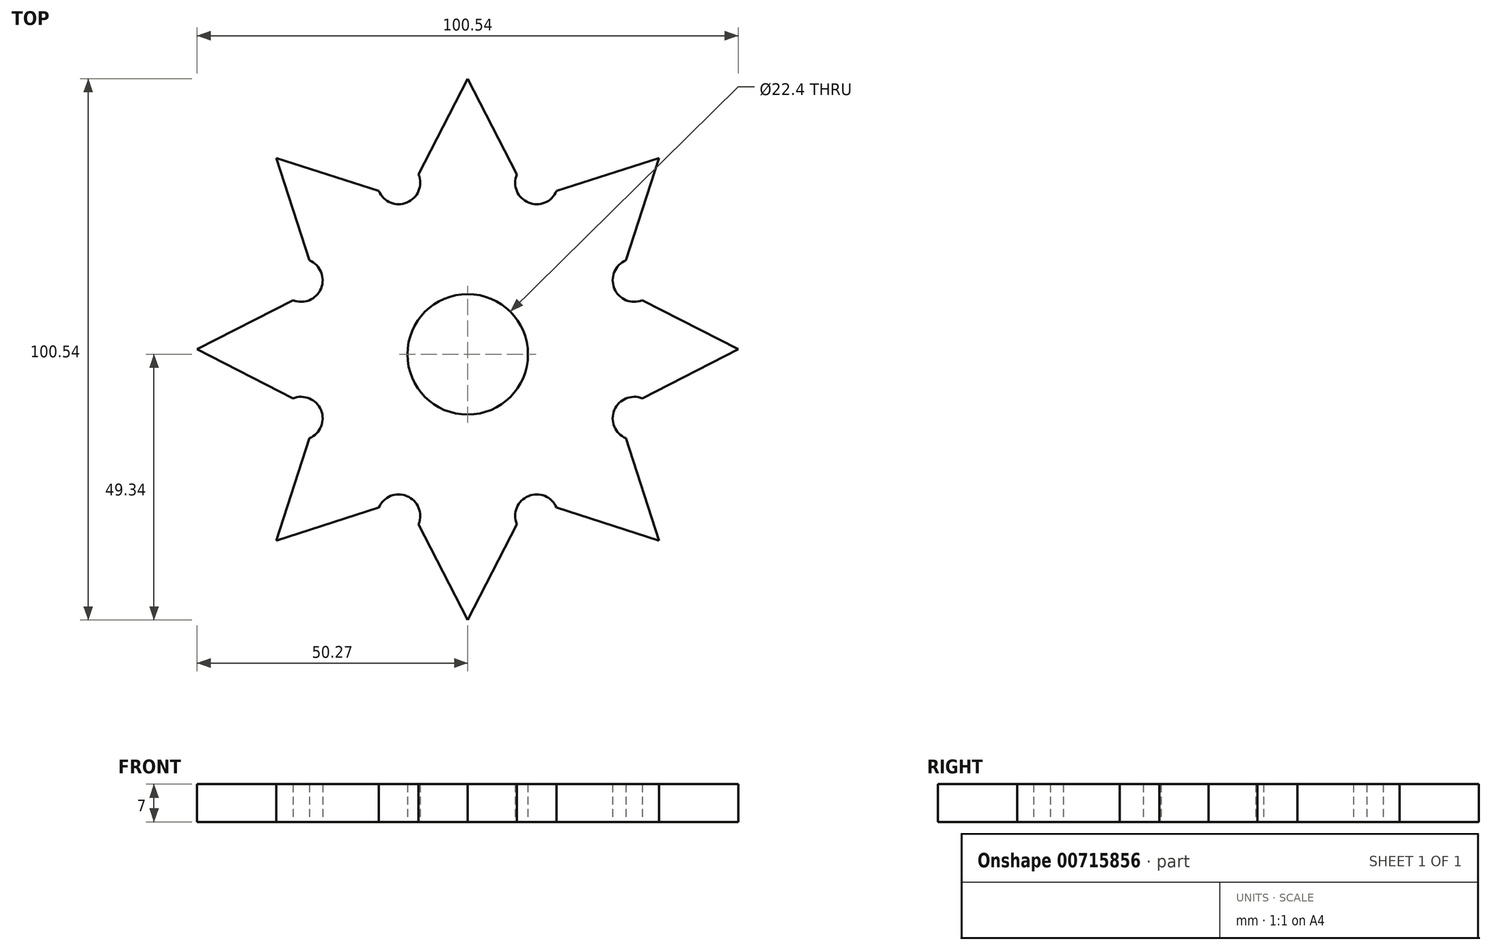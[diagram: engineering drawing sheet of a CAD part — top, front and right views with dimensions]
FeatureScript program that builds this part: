
annotation { "Feature Type Name" : "Feature", "Feature Type Description" : "" }
export const myFeature = defineFeature(function(context is Context, id is Id, definition is map)
    precondition{}
    {
        {
            var Q0;
            Q0=qCreatedBy(makeId("Top.planeOp"),FACE);
            var sketch = newSketch(context, id + "F0", { "sketchPlane" : qUnion([Q0])});
            skCircle(sketch, "E0", {"center": v(0, 0) * mm, "radius": 11.2 * mm});
            skLineSegment(sketch, "E1", {"start": v(0, 11.2) * mm, "end": v(0, 51.2) * mm});
            skLineSegment(sketch, "E2", {"start": v(0, 51.2) * mm, "end": v(9.12, 33.4) * mm});
            skLineSegment(sketch, "E3", {"start": v(0, 51.2) * mm, "end": v(-9.12, 33.4) * mm});
            skLineSegment(sketch, "E4", {"start": v(-9.12, 33.4) * mm, "end": v(0, 11.2) * mm});
            skLineSegment(sketch, "E5", {"start": v(9.12, 33.4) * mm, "end": v(0, 11.2) * mm});
            skLineSegment(sketch, "E6.1.0", {"start": v(-29.4, 17.44) * mm, "end": v(-7.26, 8.2) * mm});
            skLineSegment(sketch, "E6.1.1", {"start": v(-16.51, 30.34) * mm, "end": v(-7.26, 8.2) * mm});
            skLineSegment(sketch, "E6.1.2", {"start": v(-35.54, 36.48) * mm, "end": v(-16.51, 30.34) * mm});
            skLineSegment(sketch, "E6.1.3", {"start": v(-35.54, 36.48) * mm, "end": v(-29.4, 17.44) * mm});
            skLineSegment(sketch, "E6.2.0", {"start": v(-32.47, -8.19) * mm, "end": v(-10.27, 0.93) * mm});
            skLineSegment(sketch, "E6.2.1", {"start": v(-32.47, 10.05) * mm, "end": v(-10.27, 0.93) * mm});
            skLineSegment(sketch, "E6.2.2", {"start": v(-50.27, 0.93) * mm, "end": v(-32.47, 10.05) * mm});
            skLineSegment(sketch, "E6.2.3", {"start": v(-50.27, 0.93) * mm, "end": v(-32.47, -8.19) * mm});
            skLineSegment(sketch, "E6.3.0", {"start": v(-16.51, -28.47) * mm, "end": v(-7.26, -6.33) * mm});
            skLineSegment(sketch, "E6.3.1", {"start": v(-29.4, -15.58) * mm, "end": v(-7.26, -6.33) * mm});
            skLineSegment(sketch, "E6.3.2", {"start": v(-35.54, -34.61) * mm, "end": v(-29.4, -15.58) * mm});
            skLineSegment(sketch, "E6.3.3", {"start": v(-35.54, -34.61) * mm, "end": v(-16.51, -28.47) * mm});
            skLineSegment(sketch, "E6.4.0", {"start": v(9.12, -31.54) * mm, "end": v(0, -9.34) * mm});
            skLineSegment(sketch, "E6.4.1", {"start": v(-9.12, -31.54) * mm, "end": v(0, -9.34) * mm});
            skLineSegment(sketch, "E6.4.2", {"start": v(0, -49.34) * mm, "end": v(-9.12, -31.54) * mm});
            skLineSegment(sketch, "E6.4.3", {"start": v(0, -49.34) * mm, "end": v(9.12, -31.54) * mm});
            skLineSegment(sketch, "E6.5.0", {"start": v(29.4, -15.58) * mm, "end": v(7.26, -6.33) * mm});
            skLineSegment(sketch, "E6.5.1", {"start": v(16.51, -28.47) * mm, "end": v(7.26, -6.33) * mm});
            skLineSegment(sketch, "E6.5.2", {"start": v(35.54, -34.61) * mm, "end": v(16.51, -28.47) * mm});
            skLineSegment(sketch, "E6.5.3", {"start": v(35.54, -34.61) * mm, "end": v(29.4, -15.58) * mm});
            skLineSegment(sketch, "E6.6.0", {"start": v(32.47, 10.05) * mm, "end": v(10.27, 0.93) * mm});
            skLineSegment(sketch, "E6.6.1", {"start": v(32.47, -8.19) * mm, "end": v(10.27, 0.93) * mm});
            skLineSegment(sketch, "E6.6.2", {"start": v(50.27, 0.93) * mm, "end": v(32.47, -8.19) * mm});
            skLineSegment(sketch, "E6.6.3", {"start": v(50.27, 0.93) * mm, "end": v(32.47, 10.05) * mm});
            skLineSegment(sketch, "E6.7.0", {"start": v(16.51, 30.34) * mm, "end": v(7.26, 8.2) * mm});
            skLineSegment(sketch, "E6.7.1", {"start": v(29.4, 17.44) * mm, "end": v(7.26, 8.2) * mm});
            skLineSegment(sketch, "E6.7.2", {"start": v(35.54, 36.48) * mm, "end": v(29.4, 17.44) * mm});
            skLineSegment(sketch, "E6.7.3", {"start": v(35.54, 36.48) * mm, "end": v(16.51, 30.34) * mm});
            skPoint(sketch, "E6.center", {"position": v(0, 0.93) * mm});
            skArc(sketch, "E7", {"start": v(-16.51, 30.34) * mm, "mid": v(-11.29, 28.18) * mm, "end": v(-9.12, 33.4) * mm});
            skArc(sketch, "E8", {"start": v(9.12, 33.4) * mm, "mid": v(11.29, 28.18) * mm, "end": v(16.51, 30.34) * mm});
            skArc(sketch, "E9", {"start": v(29.4, 17.44) * mm, "mid": v(27.25, 12.22) * mm, "end": v(32.47, 10.05) * mm});
            skArc(sketch, "E10", {"start": v(32.47, -8.19) * mm, "mid": v(27.25, -10.36) * mm, "end": v(29.4, -15.58) * mm});
            skArc(sketch, "E11", {"start": v(16.51, -28.47) * mm, "mid": v(11.29, -26.32) * mm, "end": v(9.12, -31.54) * mm});
            skArc(sketch, "E12", {"start": v(-9.12, -31.54) * mm, "mid": v(-11.29, -26.32) * mm, "end": v(-16.51, -28.47) * mm});
            skArc(sketch, "E13", {"start": v(-29.4, -15.58) * mm, "mid": v(-27.25, -10.36) * mm, "end": v(-32.47, -8.19) * mm});
            skArc(sketch, "E14", {"start": v(-32.47, 10.05) * mm, "mid": v(-27.25, 12.22) * mm, "end": v(-29.4, 17.44) * mm});
            skSolve(sketch);
        }
        {
            var Q0;
            Q0 = qSketchRegion(id + "F0", true);
            extrude(context, id + "F1", {"entities" : qUnion([Q0]), "depth" : 7 * mm, "offsetDistance" : 25 * mm});
        }
    });
